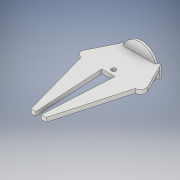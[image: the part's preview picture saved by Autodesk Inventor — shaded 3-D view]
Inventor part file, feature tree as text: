
AUTODESK INVENTOR PART (.ipt)
format: ipt  version: 2017 (Build 210142000, 142)  size: 157,696 bytes
history: native  units: in
note: dims shown in document units (in); Inventor stores cm internally (conversion verified against a paired STEP export)
features: extrude x5, sketch x5, plane x2
ambient origin geometry x8: Origin, YZ Plane, XZ Plane, XY Plane, X Axis, Y Axis, Z Axis, Center Point
bodies: Solid1 (feature_tree)
feature tree (12):
  extrude  "Extrusion1"  Depth=0.0984in TaperAngle=0.0deg
  plane  "Work Plane1"
  extrude  "Extrusion2"  Depth=1.4961in TaperAngle=0.0deg
  plane  "Work Plane2"
  extrude  "Extrusion5"  Depth=0.1969in
  sketch  "Sketch7"  dims[d36=0.1969in d37=0.0in d38=0.1969in d39=0.0in]
  sketch  "Sketch8"
  extrude  "Extrusion6"  Depth=0.1969in TaperAngle=0.0deg
  extrude  "Extrusion7"  [1 undecoded]
  sketch  "Sketch2"  dims[d0=0.2165in d1=0.0984in d2=0.0in]
  sketch  "Sketch3"  dims[d3=0.1969in d4=1.4961in d5=0.0in]
  sketch  "Sketch6"  dims[d24=0.1969in d25=0.0in d35=0.2165in]
note: 1 required parameter value undecoded (feature->parameter linkage not recoverable at this tier; creation-order binding heuristic only, values carry confidence <= 0.55)
